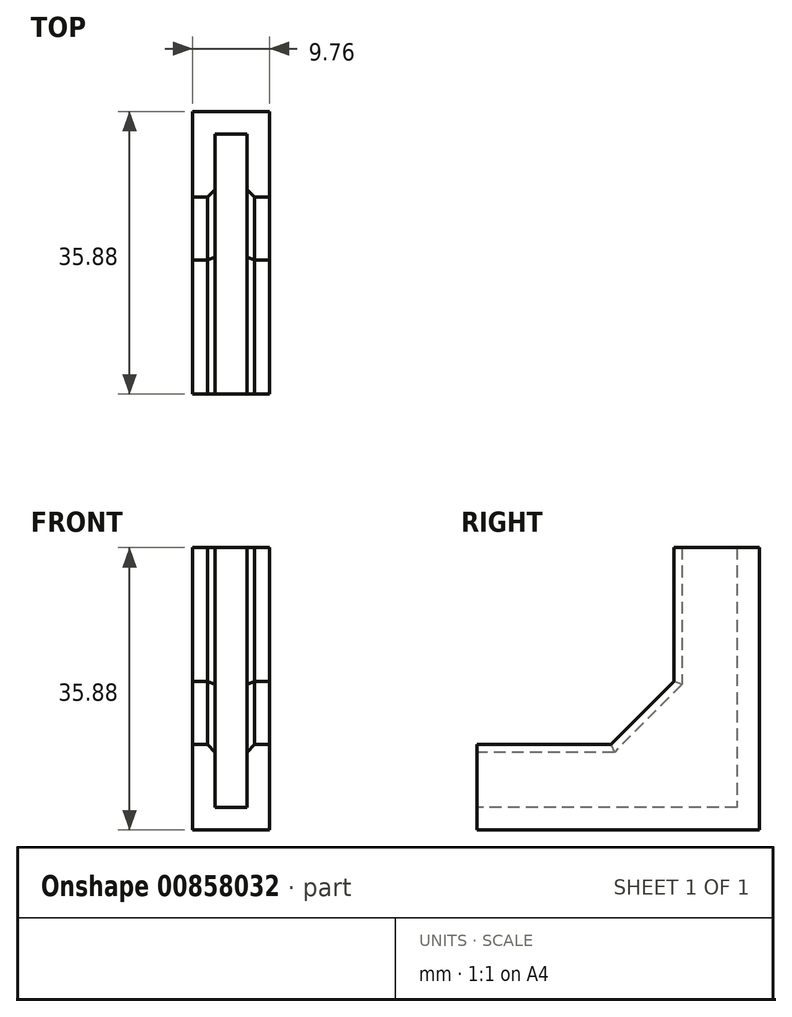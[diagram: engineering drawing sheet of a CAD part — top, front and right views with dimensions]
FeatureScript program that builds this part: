
annotation { "Feature Type Name" : "Feature", "Feature Type Description" : "" }
export const myFeature = defineFeature(function(context is Context, id is Id, definition is map)
    precondition{}
    {
        {
            var Q0;
            Q0=qCreatedBy(makeId("Right.planeOp"),FACE);
            var sketch = newSketch(context, id + "F0", { "sketchPlane" : qUnion([Q0])});
            skLineSegment(sketch, "E0", {"start": v(0, 0) * mm, "end": v(-25, 0) * mm});
            skLineSegment(sketch, "E1", {"start": v(0, 0) * mm, "end": v(0, 25) * mm});
            skSolve(sketch);
        }
        {
            var Q0;
            Q0=qCreatedBy(makeId("Front.planeOp"),FACE);
            var sketch = newSketch(context, id + "F1", { "sketchPlane" : qUnion([Q0])});
            skLineSegment(sketch, "E2", {"start": v(-2, 0) * mm, "end": v(-2, -8) * mm});
            skLineSegment(sketch, "E3", {"start": v(-2, -8) * mm, "end": v(2, -8) * mm});
            skLineSegment(sketch, "E4", {"start": v(2, -8) * mm, "end": v(2, 0) * mm});
            skLineSegment(sketch, "E5", {"start": v(2, 0) * mm, "end": v(4.88, 0) * mm});
            skLineSegment(sketch, "E6", {"start": v(4.88, 0) * mm, "end": v(4.88, -10.88) * mm});
            skLineSegment(sketch, "E7", {"start": v(4.88, -10.88) * mm, "end": v(-4.88, -10.88) * mm});
            skLineSegment(sketch, "E8", {"start": v(-4.88, -10.88) * mm, "end": v(-4.88, 0) * mm});
            skLineSegment(sketch, "E9", {"start": v(-4.88, 0) * mm, "end": v(-2, 0) * mm});
            skPoint(sketch, "E10", {"position": v(0, -8) * mm});
            skLineSegment(sketch, "E11", {"start": v(0, -8) * mm, "end": v(0, -10.88) * mm, "construction": true});
            skSolve(sketch);
        }
        {
            var Q0;
            Q0=makeQuery(id+"F1.imprint","IMPRINT",FACE,{"disambiguationData":[TD([[makeQuery(id+"F1.imprint","IMPRINT",EDGE,{"derivedFrom":sQuery(id+"F1.wireOp",EDGE,"E2")}),-1.0]])]});
            var Q1;
            Q1=sQuery(id+"F0.wireOp",EDGE,"E0");
            var Q2;
            Q2=sQuery(id+"F0.wireOp",EDGE,"E1");
            sweep(context, id + "F2", {"profiles" : qUnion([Q0]), "path" : qUnion([Q1, Q2])});
        }
        {
            var Q0;
            Q0=makeQuery(id+"F2.opSweep","MID_CAP_EDGE",EDGE,{"disambiguationData":[OSD([sQuery(id+"F0.wireOp",VERTEX,"E1.start"),sQuery(id+"F1.wireOp",EDGE,"E9")])],"capPos":1.0});
            var Q1;
            Q1=makeQuery(id+"F2.opSweep","MID_CAP_EDGE",EDGE,{"disambiguationData":[OSD([sQuery(id+"F0.wireOp",VERTEX,"E1.start"),sQuery(id+"F1.wireOp",EDGE,"E5")])],"capPos":1.0});
            chamfer(context, id + "F3", {"entities" : qUnion([Q0, Q1]), "width" : 8 * mm, "tangentPropagation" : true});
        }
        {
            var Q0;
            Q0=makeQuery(id+"F2.opSweep","SWEPT_EDGE",EDGE,{"disambiguationData":[OSD([sQuery(id+"F0.wireOp",EDGE,"E0"),sQuery(id+"F1.wireOp",EDGE,"E2"),sQuery(id+"F1.wireOp",EDGE,"E9")])]});
            var Q1;
            Q1=makeQuery(id+"F2.opSweep","SWEPT_EDGE",EDGE,{"disambiguationData":[OSD([sQuery(id+"F0.wireOp",EDGE,"E1"),sQuery(id+"F1.wireOp",EDGE,"E2"),sQuery(id+"F1.wireOp",EDGE,"E9")])]});
            var Q2;
            Q2=makeQuery(id+"F2.opSweep","SWEPT_EDGE",EDGE,{"disambiguationData":[OSD([sQuery(id+"F0.wireOp",EDGE,"E1"),sQuery(id+"F1.wireOp",EDGE,"E4"),sQuery(id+"F1.wireOp",EDGE,"E5")])]});
            var Q3;
            Q3=makeQuery(id+"F2.opSweep","SWEPT_EDGE",EDGE,{"disambiguationData":[OSD([sQuery(id+"F0.wireOp",EDGE,"E0"),sQuery(id+"F1.wireOp",EDGE,"E4"),sQuery(id+"F1.wireOp",EDGE,"E5")])]});
            var Q4;
            Q4=makeQuery(id+"F3.opChamfer","BLEND_EDGE",EDGE,{"blendedFrom":[makeQuery(id+"F2.opSweep","MID_CAP_EDGE",EDGE,{"disambiguationData":[OSD([sQuery(id+"F0.wireOp",VERTEX,"E1.start"),sQuery(id+"F1.wireOp",EDGE,"E9")])],"capPos":1.0}),makeQuery(id+"F2.opSweep","SWEPT_FACE",FACE,{"disambiguationData":[OSD([sQuery(id+"F0.wireOp",EDGE,"E1"),sQuery(id+"F1.wireOp",EDGE,"E2")])]})],"blendedInto":[makeQuery(id+"F2.opSweep","SWEPT_FACE",FACE,{"disambiguationData":[OSD([sQuery(id+"F0.wireOp",EDGE,"E1"),sQuery(id+"F1.wireOp",EDGE,"E2")])]})]});
            var Q5;
            Q5=makeQuery(id+"F3.opChamfer","BLEND_EDGE",EDGE,{"blendedFrom":[makeQuery(id+"F2.opSweep","MID_CAP_EDGE",EDGE,{"disambiguationData":[OSD([sQuery(id+"F0.wireOp",VERTEX,"E1.start"),sQuery(id+"F1.wireOp",EDGE,"E5")])],"capPos":1.0}),makeQuery(id+"F2.opSweep","SWEPT_FACE",FACE,{"disambiguationData":[OSD([sQuery(id+"F0.wireOp",EDGE,"E1"),sQuery(id+"F1.wireOp",EDGE,"E4")])]})],"blendedInto":[makeQuery(id+"F2.opSweep","SWEPT_FACE",FACE,{"disambiguationData":[OSD([sQuery(id+"F0.wireOp",EDGE,"E1"),sQuery(id+"F1.wireOp",EDGE,"E4")])]})]});
            chamfer(context, id + "F4", {"entities" : qUnion([Q0, Q1, Q2, Q3, Q4, Q5]), "width" : 1 * mm, "tangentPropagation" : true});
        }
    });
